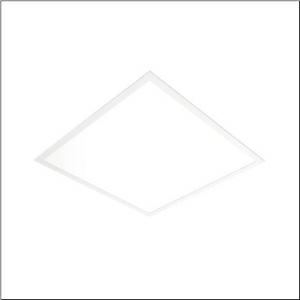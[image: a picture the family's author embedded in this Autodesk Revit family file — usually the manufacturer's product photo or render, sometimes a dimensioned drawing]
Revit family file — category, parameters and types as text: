
# Revit family: apollon_r__41_51mh11w72343_11b4
name_source: partatom
category: Lighting Fixtures
units: mm (PartAtom-declared; Revit-internal decimal feet)

## family parameters
Cut with Voids When Loaded = No
Host = Face
Light Source = No
Part Type = Normal
Room Calculation Point = No
Round Connector Dimension = Use Diameter
Shared = No

## types (1)
- Apollon® 41 (1 x LED, 3500 lm, 28.5 W, 3000K)
    Apparent Load = 29 VA
    CIE Flux Codes = 61 87 97 100 100
    Color Rendering = 80
    Color Temperature = 3000K
    Default Elevation = 1800 mm
    Description = Apollon® 41, office luminaire, primary optical cover: prismatic diffuser, of PS, light emission: direct distribution, primary light characteristic: symmetric, installation type: lay-in mounting, LED, rated luminous flux: 3.500lm, luminous efficacy: 123lm/W, light colour: 830, colour temperature: 3000K, control gear: ON/OFF, with terminal, 3-pole, mains connection: 220..240V, AC, 50/60Hz, housing, of aluminium section, traffic white (RAL 9016), module: M625, length: 620mm, width: 620mm, height: 60mm, recess depth: 180mm, housing upper side, of sheet steel, protection rating (complete): IP20, protection rating (lamp compartment, on room side): IP40, insulation class (complete): insulation class II (safety insulation), certification: CE, ENEC, impact resistance: IK03, permissible operating ambient temperature: -25..+40°C, packaging unit: 1 piece
    Height = 0 mm  [stored 0 ft]
    Lamp = 1 x LED
    Lamp Light Flux = 3500 lm
    Lamp Power = 28.5 W
    Lamp count = 1
    Length = 620 mm
    Luminous efficacy = 123 lm/W
    Manufacturer = Siteco
    ModVariant = No
    Model = 51MH11W72343
    Mounting Place = Ceiling
    Mounting Type = Recessed
    Number of Poles = 1
    OnlyDefault = Yes
    Power Factor = 1
    Product Name = Apollon® 41
    Product group = office luminaire | ceiling recessed
    ProductGroupID = 401
    Protection Class = Protection class II
    Protection Degree = IP 20
    RLX_Detail_Level = 1
    RLX_Emergency_Light_Flux = 0 lm
    RLX_Emergency_Type = 0
    RLX_Emergency_Type_DB = No
    RlxData = <blob elided: 12265 chars, md5=39ff36b1>
    Socket = socket
    Standby Power = 0 W
    System Light Flux = 3500 lm
    System Power = 29 W
    Type Comments = Product without accessories
    Type Image = l_1291024.jpg
    URL = http://relux.com
    VarID = ---
    Voltage = 0 V
    Weight = 0.00 kg
    Width = 620 mm

note: [stored X ft] marks values corroborated as IEEE doubles in the binary element streams (Revit-internal decimal feet)

## geometry (parser evidence)
native form markers: Sweep x10
no freeform markers — native parametric forms only
